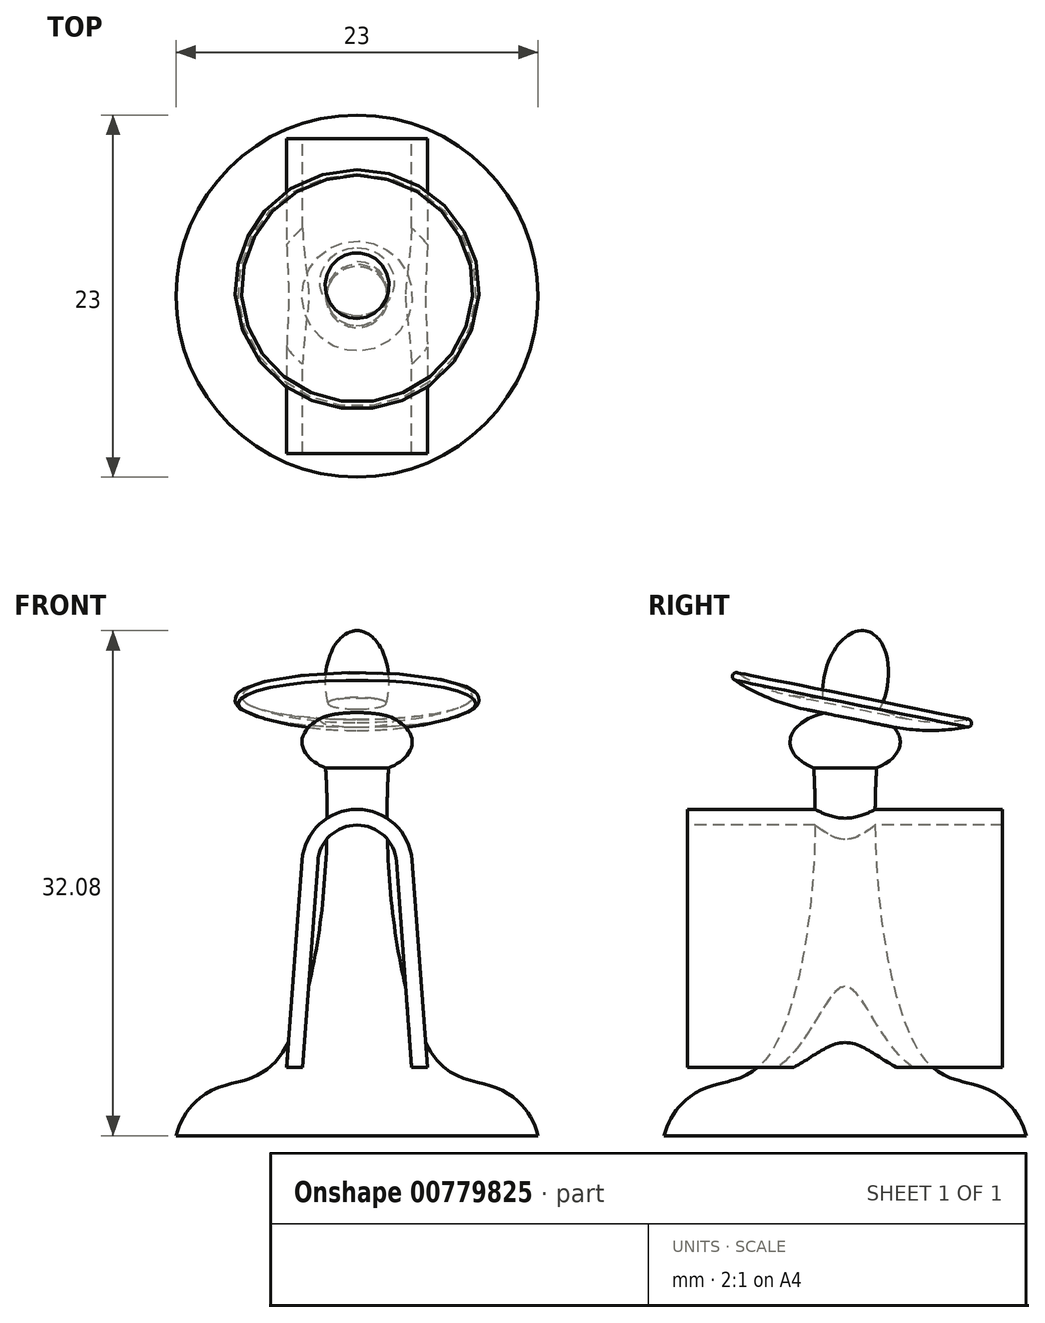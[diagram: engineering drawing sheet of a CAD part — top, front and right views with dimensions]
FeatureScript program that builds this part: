
annotation { "Feature Type Name" : "Feature", "Feature Type Description" : "" }
export const myFeature = defineFeature(function(context is Context, id is Id, definition is map)
    precondition{}
    {
        {
            var Q0;
            Q0=qCreatedBy(makeId("Front.planeOp"),FACE);
            var sketch = newSketch(context, id + "F0", { "sketchPlane" : qUnion([Q0])});
            skLineSegment(sketch, "E0", {"start": v(0, 0) * mm, "end": v(0, 27) * mm});
            skEllipticalArc(sketch, "E1", {});
            skLineSegment(sketch, "E2", {"start": v(0, 0) * mm, "end": v(11.5, 0) * mm});
            skLineSegment(sketch, "E3.0", {"start": v(2, 0) * mm, "end": v(2, 25) * mm, "construction": true});
            skFitSpline(sketch, "E4", {"points": [v(2, 23.36) * mm, v(5.13, 4.74) * mm, v(8.7, 3.1) * mm, v(10.7, 1.65) * mm, v(11.5, 0) * mm], "startDerivative": vector(-2.9, -44.3) * mm, "endDerivative": vector(3.99, -13.24) * mm});
            const initialGuessF0  = {"E1": [0, 0.025, 1, 0, 0.0035, 0.002, 5.3206345592948985, 1.5707963267948966]};
            skSetInitialGuess(sketch, initialGuessF0);
            skSolve(sketch);
        }
        {
            var Q0;
            Q0=makeQuery(id+"F0.imprint","IMPRINT",FACE,{"disambiguationData":[TD([[makeQuery(id+"F0.imprint","IMPRINT",EDGE,{"derivedFrom":sQuery(id+"F0.wireOp",EDGE,"E0")}),-1.0]])]});
            var Q1;
            Q1=sQuery(id+"F0.wireOp",EDGE,"E0");
            revolve(context, id + "F1", {"entities" : qUnion([Q0]), "axis" : qUnion([Q1]), "revolveType" : RevolveType.FULL});
        }
        {
            var Q0;
            Q0=qCreatedBy(makeId("Front.planeOp"),FACE);
            var sketch = newSketch(context, id + "F2", { "sketchPlane" : qUnion([Q0])});
            skLineSegment(sketch, "E5.0", {"start": v(0, 0) * mm, "end": v(0, 14.73) * mm, "construction": true});
            skArc(sketch, "E6", {"start": v(3.5, 17.49) * mm, "mid": v(2.38, 19.8) * mm, "end": v(0, 20.73) * mm});
            skLineSegment(sketch, "E7", {"start": v(3.47, 4.35) * mm, "end": v(4.47, 4.35) * mm});
            skLineSegment(sketch, "E8", {"start": v(3.5, 17.49) * mm, "end": v(4.47, 4.35) * mm});
            skLineSegment(sketch, "E9.0", {"start": v(2.5, 17.41) * mm, "end": v(3.47, 4.27) * mm});
            skArc(sketch, "E10", {"start": v(2.5, 17.41) * mm, "mid": v(1.7, 19.06) * mm, "end": v(0, 19.73) * mm});
            skLineSegment(sketch, "E11.trimOffspring", {"start": v(0, 19.73) * mm, "end": v(0, 27) * mm, "construction": true});
            skPoint(sketch, "E12.orphan", {"position": v(0, 4.35) * mm});
            skPoint(sketch, "E13.orphan", {"position": v(8.94, 4.35) * mm});
            skLineSegment(sketch, "E14.MirrorCS", {"start": v(-2.5, 17.41) * mm, "end": v(-3.47, 4.27) * mm});
            skLineSegment(sketch, "E15.MirrorCS", {"start": v(-3.47, 4.35) * mm, "end": v(-4.47, 4.35) * mm});
            skLineSegment(sketch, "E16.MirrorCS", {"start": v(-3.5, 17.49) * mm, "end": v(-4.47, 4.35) * mm});
            skArc(sketch, "E17.MirrorCS", {"start": v(-3.5, 17.49) * mm, "mid": v(-2.38, 19.8) * mm, "end": v(0, 20.73) * mm});
            skArc(sketch, "E18.MirrorCS", {"start": v(-2.5, 17.41) * mm, "mid": v(-1.7, 19.06) * mm, "end": v(0, 19.73) * mm});
            skSolve(sketch);
        }
        {
            var Q0;
            Q0=makeQuery(id+"F2.imprint","IMPRINT",FACE,{"disambiguationData":[TD([[makeQuery(id+"F2.imprint","IMPRINT",EDGE,{"derivedFrom":sQuery(id+"F2.wireOp",EDGE,"E6")}),1.0]])]});
            extrude(context, id + "F3", {"entities" : qUnion([Q0]), "operationType" : NewBodyOperationType.ADD, "endBound" : BoundingType.SYMMETRIC, "depth" : 20 * mm, "offsetDistance" : 25 * mm, "hasDraft" : true, "draftAngle" : 0 * degree});
        }
        {
            var Q0;
            Q0=qCreatedBy(makeId("Right.planeOp"),FACE);
            var sketch = newSketch(context, id + "F4", { "sketchPlane" : qUnion([Q0])});
            skLineSegment(sketch, "E19", {"start": v(0, 25.51) * mm, "end": v(1.32, 32.06) * mm});
            skPoint(sketch, "E20.startSnap0", {"position": v(0.66, 28.79) * mm});
            skEllipticalArc(sketch, "E21", {});
            skArc(sketch, "E22", {"start": v(-7, 28.93) * mm, "mid": v(-4.25, 27.56) * mm, "end": v(-1.25, 26.88) * mm});
            skArc(sketch, "E23", {"start": v(-6.72, 29.33) * mm, "mid": v(-4.2, 28.13) * mm, "end": v(-1.43, 27.83) * mm});
            skArc(sketch, "E24", {"start": v(-6.72, 29.33) * mm, "mid": v(-7.12, 29.3) * mm, "end": v(-7, 28.93) * mm});
            skEllipticalArc(sketch, "E25.trimOffspring", {});
            const initialGuessF4  = {"E21": [0.0006584447692148367, 0.028786322101950645, 0.19732019905613693, 0.980339093908045, 0.0033369354600514783, 0.002027530294423876, 0, 1.9871585271084258], "E25.trimOffspring": [0.0006584447692148367, 0.028786322101950645, 0.19732019905613693, 0.980339093908045, 0.0033369354600514783, 0.002027530294423876, 2.3110236064606444, 3.141592653589793]};
            skSetInitialGuess(sketch, initialGuessF4);
            skSolve(sketch);
        }
        {
            var Q0;
            Q0=makeQuery(id+"F4.imprint","IMPRINT",FACE,{"disambiguationData":[TD([[makeQuery(id+"F4.imprint","IMPRINT",EDGE,{"derivedFrom":sQuery(id+"F4.wireOp",EDGE,"E19")}),1.0]])]});
            var Q1;
            Q1 = qConstructionFilter(qBodyType(qCreatedBy(id + "F4" ,EDGE), BodyType.WIRE), ConstructionObject.NO);
            var Q2;
            Q2=sQuery(id+"F4.wireOp",EDGE,"E19");
            revolve(context, id + "F5", {"operationType" : NewBodyOperationType.ADD, "surfaceOperationType" : NewSurfaceOperationType.ADD, "entities" : qUnion([Q0]), "surfaceEntities" : qUnion([Q1]), "axis" : qUnion([Q2]), "revolveType" : RevolveType.FULL});
        }
    });
